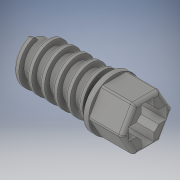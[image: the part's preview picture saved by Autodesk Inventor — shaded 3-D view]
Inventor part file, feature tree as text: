
AUTODESK INVENTOR PART (.ipt)
format: ipt  version: 2017 (Build 210142000, 142)  size: 556,544 bytes
history: native  units: in
note: dims shown in document units (in); Inventor stores cm internally (conversion verified against a paired STEP export)
features: sketch x5, extrude x4, fillet x3, plane x1, helix x1, chamfer x1, hole x1
ambient origin geometry x8: Origin, YZ Plane, XZ Plane, XY Plane, X Axis, Y Axis, Z Axis, Center Point
bodies: Solid1 (feature_tree)
feature tree (16):
  plane  "Work Plane1"
  extrude  "Screw_head"  Depth=0.5118in TaperAngle=0.0deg
  extrude  "Cross"  Depth=0.1969in
  extrude  "Extrusion7"  Depth=0.7874in TaperAngle=90.0deg
  extrude  "Extrusion8"  Depth=0.3937in TaperAngle=0.0deg
  helix  "Coil1"  [1 undecoded]
  chamfer  "Chamfer1"  Distance=0.0787in
  fillet  "Fillet1"  Radius=0.5118in
  fillet  "Fillet2"  Radius=1.1811in
  fillet  "Fillet3"  Radius=0.0787in
  hole  "Hole1"  [1 undecoded]
  sketch  "Sketch3"  dims[d0=0.7874in d7=0.5118in d8=0.0in]
  sketch  "Sketch7"  dims[d28=0.7874in d29=0.1969in]
  sketch  "Sketch8"  dims[d30=0.5906in d31=0.7874in d33=90.0deg]
  sketch  "Sketch9"  dims[d35=0.3937in d36=0.3937in d37=0.0in d38=0.7874in d39=0.0787in d40=0.0in d41=0.5118in d42=1.1811in d43=0.0in d44=0.0787in]
  sketch  "Sketch10"  dims[d45=0.0787in d46=0.0in d47=0.0in d48=0.1969in d49=0.3937in d50=2.2047in d51=0.0in d52=90.0deg d53=90.0deg d54=0.0in d55=0.0in d56=0.0315in d57=0.063in d58=0.0492in d59=45.0deg d60=0.0197in d61=0.0591in d62=0.3937in d63=0.3937in d64=0.1969in d65=0.2953in d66=0.1476in d67=0.0984in d68=90.0deg d69=0.3937in d70=0.8108in]
note: 2 required parameter values undecoded (feature->parameter linkage not recoverable at this tier; creation-order binding heuristic only, values carry confidence <= 0.55)
